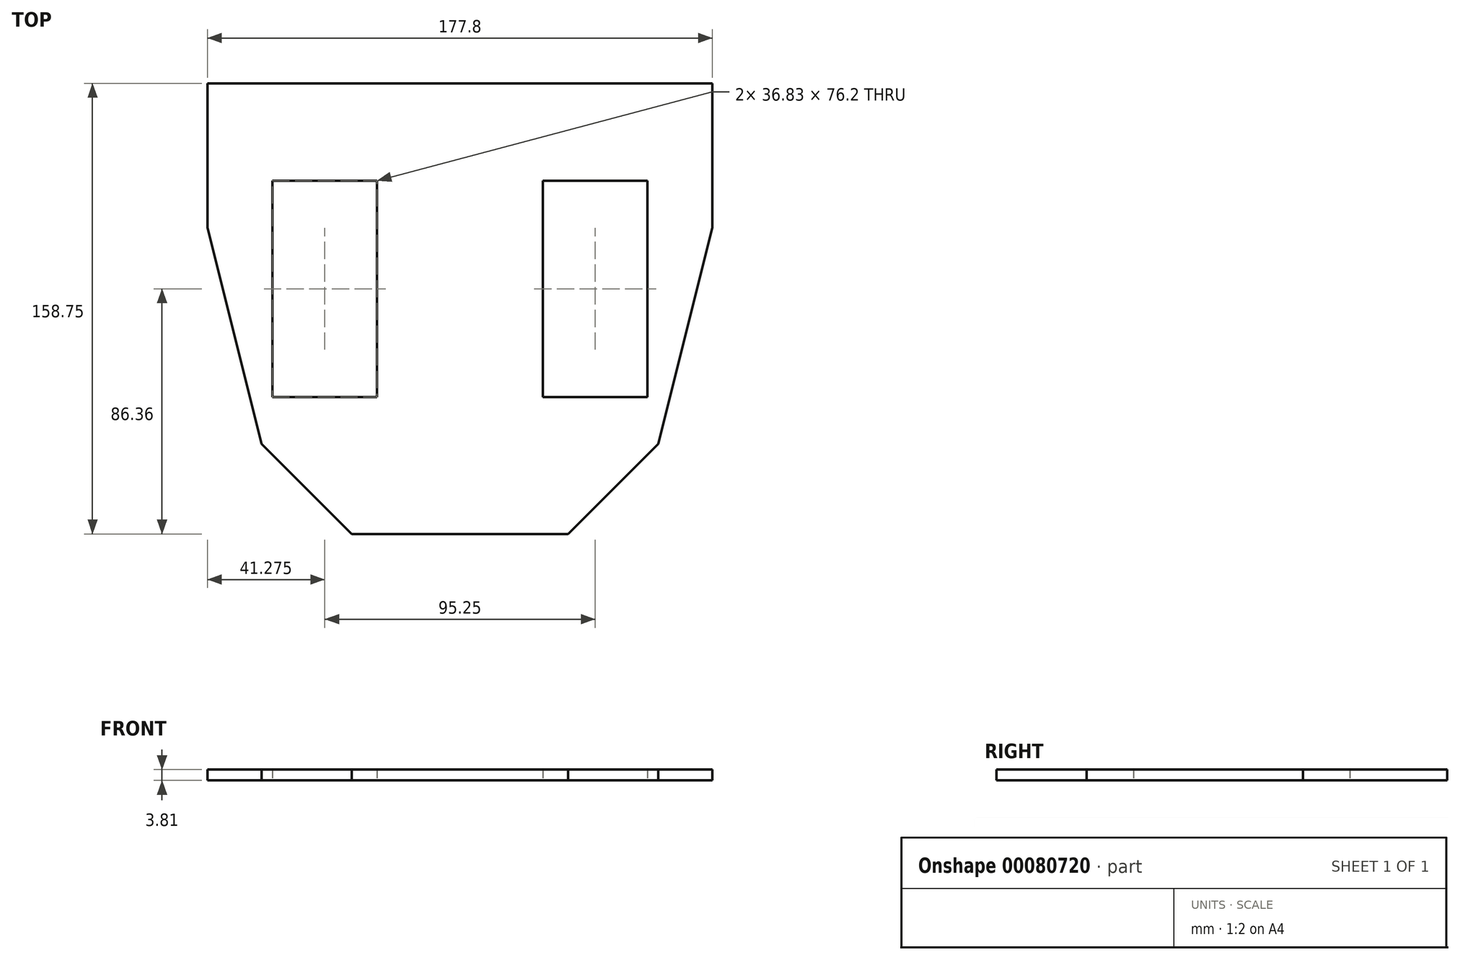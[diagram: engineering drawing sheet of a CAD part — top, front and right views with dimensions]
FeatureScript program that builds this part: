
annotation { "Feature Type Name" : "Feature", "Feature Type Description" : "" }
export const myFeature = defineFeature(function(context is Context, id is Id, definition is map)
    precondition{}
    {
        {
            var Q0;
            Q0=qCreatedBy(makeId("Top.planeOp"),FACE);
            var sketch = newSketch(context, id + "F0", { "sketchPlane" : qUnion([Q0])});
            skLineSegment(sketch, "E0", {"start": v(0, 50.8) * mm, "end": v(-88.9, 50.8) * mm});
            skLineSegment(sketch, "E1", {"start": v(0, 50.8) * mm, "end": v(88.9, 50.8) * mm});
            skLineSegment(sketch, "E2", {"start": v(0, 0) * mm, "end": v(-88.9, 0) * mm, "construction": true});
            skLineSegment(sketch, "E3", {"start": v(0, 0) * mm, "end": v(88.9, 0) * mm, "construction": true});
            skLineSegment(sketch, "E4", {"start": v(-88.9, 50.8) * mm, "end": v(-88.9, 0) * mm});
            skLineSegment(sketch, "E5", {"start": v(88.9, 50.8) * mm, "end": v(88.9, 0) * mm});
            skLineSegment(sketch, "E6", {"start": v(0, -76.2) * mm, "end": v(-69.85, -76.2) * mm, "construction": true});
            skLineSegment(sketch, "E7", {"start": v(0, -76.2) * mm, "end": v(69.85, -76.2) * mm, "construction": true});
            skLineSegment(sketch, "E8", {"start": v(-88.9, 0) * mm, "end": v(-69.85, -76.2) * mm});
            skLineSegment(sketch, "E9", {"start": v(88.9, 0) * mm, "end": v(69.85, -76.2) * mm});
            skLineSegment(sketch, "E10", {"start": v(0, -107.95) * mm, "end": v(-38.1, -107.95) * mm});
            skLineSegment(sketch, "E11", {"start": v(0, -107.95) * mm, "end": v(38.1, -107.95) * mm});
            skLineSegment(sketch, "E12", {"start": v(-69.85, -76.2) * mm, "end": v(-38.1, -107.95) * mm});
            skLineSegment(sketch, "E13", {"start": v(69.85, -76.2) * mm, "end": v(38.1, -107.95) * mm});
            skLineSegment(sketch, "E14.bottom", {"start": v(-29.21, -59.7) * mm, "end": v(-66.04, -59.69) * mm});
            skLineSegment(sketch, "E14.top", {"start": v(-29.21, 16.5) * mm, "end": v(-66.04, 16.51) * mm});
            skLineSegment(sketch, "E14.left", {"start": v(-29.21, -59.7) * mm, "end": v(-29.21, 16.5) * mm});
            skLineSegment(sketch, "E14.right", {"start": v(-66.04, -59.69) * mm, "end": v(-66.04, 16.5) * mm});
            skPoint(sketch, "E14.middle", {"position": v(-47.63, -21.6) * mm});
            skLineSegment(sketch, "E15", {"start": v(0, 50.8) * mm, "end": v(0, -107.95) * mm, "construction": true});
            skSolve(sketch);
        }
        {
            var Q0;
            Q0=makeQuery(id+"F0.imprint","IMPRINT",FACE,{"disambiguationData":[TD([[makeQuery(id+"F0.imprint","IMPRINT",EDGE,{"derivedFrom":sQuery(id+"F0.wireOp",EDGE,"E0")}),1.0]])]});
            extrude(context, id + "F1", {"entities" : qUnion([Q0]), "depth" : 3.8 * mm});
        }
        {
            var Q0;
            Q0=makeQuery(id+"F1.opExtrude","SWEPT_BODY",BODY,{"disambiguationData":[OSD([sQuery(id+"F0.wireOp",EDGE,"E0"),sQuery(id+"F0.wireOp",EDGE,"E1"),sQuery(id+"F0.wireOp",EDGE,"E4"),sQuery(id+"F0.wireOp",EDGE,"E5"),sQuery(id+"F0.wireOp",EDGE,"E8"),sQuery(id+"F0.wireOp",EDGE,"E9"),sQuery(id+"F0.wireOp",EDGE,"E10"),sQuery(id+"F0.wireOp",EDGE,"E11"),sQuery(id+"F0.wireOp",EDGE,"E12"),sQuery(id+"F0.wireOp",EDGE,"E13"),sQuery(id+"F0.wireOp",EDGE,"E14.bottom"),sQuery(id+"F0.wireOp",EDGE,"E14.top"),sQuery(id+"F0.wireOp",EDGE,"E14.left"),sQuery(id+"F0.wireOp",EDGE,"E14.right")])]});
            var Q1;
            Q1=qCreatedBy(makeId("Right.planeOp"),FACE);
            mirror(context, id + "F2", {"operationType" : NewBodyOperationType.INTERSECT, "entities" : qUnion([Q0]), "mirrorPlane" : qUnion([Q1])});
        }
    });
